annotation { "Feature Type Name" : "Feature", "Feature Type Description" : "" }
export const myFeature = defineFeature(function(context is Context, id is Id, definition is map)
    precondition{}
    {
        {
            var Q0;
            Q0=qCreatedBy(makeId("Top.planeOp"),FACE);
            var sketch = newSketch(context, id + "F0", { "sketchPlane" : qUnion([Q0])});
            skLineSegment(sketch, "E0.bottom", {"start": v(0, 0) * mm, "end": v(203.2, 0) * mm});
            skLineSegment(sketch, "E0.top", {"start": v(0, 254) * mm, "end": v(203.2, 254) * mm});
            skLineSegment(sketch, "E0.left", {"start": v(0, 0) * mm, "end": v(0, 254) * mm});
            skLineSegment(sketch, "E0.right", {"start": v(203.2, 0) * mm, "end": v(203.2, 254) * mm});
            skSolve(sketch);
        }
        {
            var Q0;
            Q0=makeQuery(id+"F0.imprint","IMPRINT",FACE,{"disambiguationData":[TD([[makeQuery(id+"F0.imprint","IMPRINT",EDGE,{"derivedFrom":sQuery(id+"F0.wireOp",EDGE,"E0.bottom")}),1.0]])]});
            extrude(context, id + "F1", {"entities" : qUnion([Q0]), "depth" : 6.35 * mm});
        }
        {
            var Q0;
            Q0=makeQuery(id+"F1.opExtrude","CAP_FACE",FACE,{"disambiguationData":[OSD([sQuery(id+"F0.wireOp",EDGE,"E0.bottom"),sQuery(id+"F0.wireOp",EDGE,"E0.top"),sQuery(id+"F0.wireOp",EDGE,"E0.left"),sQuery(id+"F0.wireOp",EDGE,"E0.right")])],"isStart":false});
            var sketch = newSketch(context, id + "F2", { "sketchPlane" : qUnion([Q0])});
            skLineSegment(sketch, "E1.bottom", {"start": v(50.8, 223.52) * mm, "end": v(152.4, 223.52) * mm});
            skLineSegment(sketch, "E1.top", {"start": v(50.8, 30.48) * mm, "end": v(152.4, 30.48) * mm});
            skLineSegment(sketch, "E1.left", {"start": v(44.45, 217.17) * mm, "end": v(44.45, 36.83) * mm});
            skLineSegment(sketch, "E1.right", {"start": v(158.75, 217.17) * mm, "end": v(158.75, 36.83) * mm});
            skPoint(sketch, "E2.visualSharp", {"position": v(44.45, 223.52) * mm});
            skArc(sketch, "E2.filletArc", {"start": v(50.8, 223.52) * mm, "mid": v(46.3, 221.66) * mm, "end": v(44.45, 217.17) * mm});
            skPoint(sketch, "E3.visualSharp", {"position": v(158.75, 223.52) * mm});
            skArc(sketch, "E3.filletArc", {"start": v(158.75, 217.17) * mm, "mid": v(156.9, 221.66) * mm, "end": v(152.4, 223.52) * mm});
            skPoint(sketch, "E4.visualSharp", {"position": v(158.75, 30.48) * mm});
            skArc(sketch, "E4.filletArc", {"start": v(152.4, 30.48) * mm, "mid": v(156.9, 32.34) * mm, "end": v(158.75, 36.83) * mm});
            skPoint(sketch, "E5.visualSharp", {"position": v(44.45, 30.48) * mm});
            skArc(sketch, "E5.filletArc", {"start": v(44.45, 36.83) * mm, "mid": v(46.3, 32.34) * mm, "end": v(50.8, 30.48) * mm});
            skSolve(sketch);
        }
        {
            var Q0;
            Q0=makeQuery(id+"F2.imprint","IMPRINT",FACE,{"disambiguationData":[TD([[makeQuery(id+"F2.imprint","IMPRINT",EDGE,{"derivedFrom":sQuery(id+"F2.wireOp",EDGE,"E1.bottom")}),-1.0]])]});
            extrude(context, id + "F3", {"entities" : qUnion([Q0]), "operationType" : NewBodyOperationType.ADD, "depth" : 50.8 * mm});
        }
        {
            var Q0;
            Q0=makeQuery(id+"F3.opExtrude","CAP_FACE",FACE,{"disambiguationData":[OSD([sQuery(id+"F2.wireOp",EDGE,"E1.bottom"),sQuery(id+"F2.wireOp",EDGE,"E1.top"),sQuery(id+"F2.wireOp",EDGE,"E1.left"),sQuery(id+"F2.wireOp",EDGE,"E1.right"),sQuery(id+"F2.wireOp",EDGE,"E2.filletArc"),sQuery(id+"F2.wireOp",EDGE,"E3.filletArc"),sQuery(id+"F2.wireOp",EDGE,"E4.filletArc"),sQuery(id+"F2.wireOp",EDGE,"E5.filletArc")])],"isStart":false});
            var sketch = newSketch(context, id + "F4", { "sketchPlane" : qUnion([Q0])});
            skLineSegment(sketch, "E6", {"start": v(101.6, 49.53) * mm, "end": v(-6.35, 49.53) * mm});
            skLineSegment(sketch, "E7", {"start": v(-6.35, 49.53) * mm, "end": v(-6.35, 328.93) * mm});
            skLineSegment(sketch, "E8", {"start": v(-6.35, 328.93) * mm, "end": v(209.55, 328.93) * mm});
            skLineSegment(sketch, "E9", {"start": v(209.55, 328.93) * mm, "end": v(209.55, 49.53) * mm});
            skLineSegment(sketch, "E10", {"start": v(101.6, 49.53) * mm, "end": v(209.55, 49.53) * mm});
            skSolve(sketch);
        }
        {
            var Q0;
            {var subQ1=sQuery(id+"F4.wireOp",EDGE,"E7");Q0=makeQuery(id+"F4.imprint","IMPRINT",FACE,{"disambiguationData":[TD([[makeQuery(id+"F4.imprint","IMPRINT",EDGE,{"derivedFrom":subQ1}),-1.0]])]});}
            var Q1;
            Q1=makeQuery(id+"F4.imprint","IMPRINT",FACE,{"disambiguationData":[TD([[makeQuery(id+"F4.imprint","IMPRINT",EDGE,{"derivedFrom":makeQuery(id+"F3.opExtrude","CAP_EDGE",EDGE,{"disambiguationData":[OSD([sQuery(id+"F2.wireOp",EDGE,"E1.bottom")])],"isStart":false})}),-1.0]])]});
            extrude(context, id + "F5", {"entities" : qUnion([Q0, Q1]), "operationType" : NewBodyOperationType.ADD, "depth" : 31.75 * mm});
        }
        {
            var Q0;
            Q0=makeQuery(id+"F5.opExtrude","SWEPT_FACE",FACE,{"disambiguationData":[OSD([sQuery(id+"F4.wireOp",EDGE,"E6"),sQuery(id+"F4.wireOp",EDGE,"E10")])]});
            var sketch = newSketch(context, id + "F6", { "sketchPlane" : qUnion([Q0])});
            skLineSegment(sketch, "E11.bottom", {"start": v(-6.35, 57.15) * mm, "end": v(209.55, 57.15) * mm});
            skLineSegment(sketch, "E11.top", {"start": v(-6.35, 82.55) * mm, "end": v(209.55, 82.55) * mm});
            skLineSegment(sketch, "E11.left", {"start": v(-6.35, 57.15) * mm, "end": v(-6.35, 82.55) * mm});
            skLineSegment(sketch, "E11.right", {"start": v(209.55, 57.15) * mm, "end": v(209.55, 82.55) * mm});
            skSolve(sketch);
        }
        {
            var Q0;
            Q0=makeQuery(id+"F6.imprint","IMPRINT",FACE,{"disambiguationData":[TD([[makeQuery(id+"F6.imprint","IMPRINT",EDGE,{"derivedFrom":sQuery(id+"F6.wireOp",EDGE,"E11.top")}),-1.0]])]});
            extrude(context, id + "F7", {"entities" : qUnion([Q0]), "operationType" : NewBodyOperationType.REMOVE, "oppositeDirection" : true, "depth" : 304.3 * mm});
        }
        {
            var Q0;
            Q0=makeQuery(id+"F5.opExtrude","CAP_FACE",FACE,{"disambiguationData":[OSD([sQuery(id+"F4.wireOp",EDGE,"E6"),sQuery(id+"F4.wireOp",EDGE,"E7"),sQuery(id+"F4.wireOp",EDGE,"E8"),sQuery(id+"F4.wireOp",EDGE,"E9"),sQuery(id+"F4.wireOp",EDGE,"E10")])],"isStart":false});
            var sketch = newSketch(context, id + "F8", { "sketchPlane" : qUnion([Q0])});
            skLineSegment(sketch, "E12.bottom", {"start": v(31.75, 62.23) * mm, "end": v(165.1, 62.23) * mm});
            skLineSegment(sketch, "E12.top", {"start": v(31.75, 204.47) * mm, "end": v(165.1, 204.47) * mm});
            skLineSegment(sketch, "E12.left", {"start": v(25.4, 68.58) * mm, "end": v(25.4, 198.12) * mm});
            skLineSegment(sketch, "E12.right", {"start": v(171.45, 68.58) * mm, "end": v(171.45, 198.12) * mm});
            skPoint(sketch, "E13.visualSharp", {"position": v(25.4, 204.47) * mm});
            skArc(sketch, "E13.filletArc", {"start": v(31.75, 204.47) * mm, "mid": v(27.26, 202.61) * mm, "end": v(25.4, 198.12) * mm});
            skPoint(sketch, "E14.visualSharp", {"position": v(171.45, 204.47) * mm});
            skArc(sketch, "E14.filletArc", {"start": v(171.45, 198.12) * mm, "mid": v(169.6, 202.61) * mm, "end": v(165.1, 204.47) * mm});
            skPoint(sketch, "E15.visualSharp", {"position": v(171.45, 62.23) * mm});
            skArc(sketch, "E15.filletArc", {"start": v(165.1, 62.23) * mm, "mid": v(169.6, 64.09) * mm, "end": v(171.45, 68.58) * mm});
            skPoint(sketch, "E16.visualSharp", {"position": v(25.4, 62.23) * mm});
            skArc(sketch, "E16.filletArc", {"start": v(25.4, 68.58) * mm, "mid": v(27.26, 64.09) * mm, "end": v(31.75, 62.23) * mm});
            skSolve(sketch);
        }
        {
            var Q0;
            Q0=makeQuery(id+"F8.imprint","IMPRINT",FACE,{"disambiguationData":[TD([[makeQuery(id+"F8.imprint","IMPRINT",EDGE,{"derivedFrom":sQuery(id+"F8.wireOp",EDGE,"E12.bottom")}),1.0]])]});
            extrude(context, id + "F9", {"entities" : qUnion([Q0]), "operationType" : NewBodyOperationType.ADD, "depth" : 25.4 * mm});
        }
        {
            var Q0;
            Q0=makeQuery(id+"F9.opExtrude","CAP_FACE",FACE,{"disambiguationData":[OSD([sQuery(id+"F8.wireOp",EDGE,"E12.bottom"),sQuery(id+"F8.wireOp",EDGE,"E12.top"),sQuery(id+"F8.wireOp",EDGE,"E12.left"),sQuery(id+"F8.wireOp",EDGE,"E12.right"),sQuery(id+"F8.wireOp",EDGE,"E13.filletArc"),sQuery(id+"F8.wireOp",EDGE,"E14.filletArc"),sQuery(id+"F8.wireOp",EDGE,"E15.filletArc"),sQuery(id+"F8.wireOp",EDGE,"E16.filletArc")])],"isStart":false});
            var sketch = newSketch(context, id + "F10", { "sketchPlane" : qUnion([Q0])});
            skLineSegment(sketch, "E17.bottom", {"start": v(63.5, 179.07) * mm, "end": v(127, 179.07) * mm});
            skLineSegment(sketch, "E17.top", {"start": v(63.5, 204.47) * mm, "end": v(127, 204.47) * mm});
            skLineSegment(sketch, "E17.left", {"start": v(63.5, 179.07) * mm, "end": v(63.5, 204.47) * mm});
            skLineSegment(sketch, "E17.right", {"start": v(127, 179.07) * mm, "end": v(127, 204.47) * mm});
            skSolve(sketch);
        }
        {
            var Q0;
            Q0=makeQuery(id+"F10.imprint","IMPRINT",FACE,{"disambiguationData":[TD([[makeQuery(id+"F10.imprint","IMPRINT",EDGE,{"derivedFrom":sQuery(id+"F10.wireOp",EDGE,"E17.bottom")}),1.0]])]});
            extrude(context, id + "F11", {"entities" : qUnion([Q0]), "operationType" : NewBodyOperationType.ADD, "depth" : 12.7 * mm});
        }
        {
            var Q0;
            Q0=makeQuery(id+"F5.opExtrude","CAP_FACE",FACE,{"disambiguationData":[OSD([sQuery(id+"F4.wireOp",EDGE,"E6"),sQuery(id+"F4.wireOp",EDGE,"E7"),sQuery(id+"F4.wireOp",EDGE,"E8"),sQuery(id+"F4.wireOp",EDGE,"E9"),sQuery(id+"F4.wireOp",EDGE,"E10")])],"isStart":false});
            var sketch = newSketch(context, id + "F12", { "sketchPlane" : qUnion([Q0])});
            skLineSegment(sketch, "E18.bottom", {"start": v(179.04, 307.91) * mm, "end": v(134.59, 307.91) * mm});
            skLineSegment(sketch, "E18.top", {"start": v(179.04, 257.11) * mm, "end": v(134.59, 257.11) * mm});
            skLineSegment(sketch, "E18.left", {"start": v(185.39, 301.56) * mm, "end": v(185.39, 263.46) * mm});
            skLineSegment(sketch, "E18.right", {"start": v(128.24, 301.56) * mm, "end": v(128.24, 263.46) * mm});
            skPoint(sketch, "E19.visualSharp", {"position": v(128.24, 307.91) * mm});
            skArc(sketch, "E19.filletArc", {"start": v(134.59, 307.91) * mm, "mid": v(130.1, 306.05) * mm, "end": v(128.24, 301.56) * mm});
            skPoint(sketch, "E20.visualSharp", {"position": v(185.39, 307.91) * mm});
            skArc(sketch, "E20.filletArc", {"start": v(185.39, 301.56) * mm, "mid": v(183.53, 306.05) * mm, "end": v(179.04, 307.91) * mm});
            skPoint(sketch, "E21.visualSharp", {"position": v(185.39, 257.11) * mm});
            skArc(sketch, "E21.filletArc", {"start": v(179.04, 257.11) * mm, "mid": v(183.53, 258.97) * mm, "end": v(185.39, 263.46) * mm});
            skPoint(sketch, "E22.visualSharp", {"position": v(128.24, 257.11) * mm});
            skArc(sketch, "E22.filletArc", {"start": v(128.24, 263.46) * mm, "mid": v(130.1, 258.97) * mm, "end": v(134.59, 257.11) * mm});
            skSolve(sketch);
        }
        {
            var Q0;
            Q0=makeQuery(id+"F12.imprint","IMPRINT",FACE,{"disambiguationData":[TD([[makeQuery(id+"F12.imprint","IMPRINT",EDGE,{"derivedFrom":sQuery(id+"F12.wireOp",EDGE,"E18.bottom")}),1.0]])]});
            extrude(context, id + "F13", {"entities" : qUnion([Q0]), "operationType" : NewBodyOperationType.ADD, "depth" : 25.4 * mm});
        }
        {
            var Q0;
            Q0=makeQuery(id+"F5.opExtrude","CAP_FACE",FACE,{"disambiguationData":[OSD([sQuery(id+"F4.wireOp",EDGE,"E6"),sQuery(id+"F4.wireOp",EDGE,"E7"),sQuery(id+"F4.wireOp",EDGE,"E8"),sQuery(id+"F4.wireOp",EDGE,"E9"),sQuery(id+"F4.wireOp",EDGE,"E10")])],"isStart":false});
            var sketch = newSketch(context, id + "F14", { "sketchPlane" : qUnion([Q0])});
            skLineSegment(sketch, "E23", {"start": v(39.34, 316.23) * mm, "end": v(83.79, 316.23) * mm});
            skLineSegment(sketch, "E24", {"start": v(90.14, 309.88) * mm, "end": v(90.14, 252.73) * mm});
            skLineSegment(sketch, "E25", {"start": v(32.99, 309.88) * mm, "end": v(32.99, 252.73) * mm});
            skLineSegment(sketch, "E26", {"start": v(39.34, 246.38) * mm, "end": v(83.79, 246.38) * mm});
            skPoint(sketch, "E27.visualSharp", {"position": v(32.99, 316.23) * mm});
            skArc(sketch, "E27.filletArc", {"start": v(39.34, 316.23) * mm, "mid": v(34.85, 314.37) * mm, "end": v(32.99, 309.88) * mm});
            skPoint(sketch, "E28.visualSharp", {"position": v(90.14, 316.23) * mm});
            skArc(sketch, "E28.filletArc", {"start": v(90.14, 309.88) * mm, "mid": v(88.28, 314.37) * mm, "end": v(83.79, 316.23) * mm});
            skPoint(sketch, "E29.visualSharp", {"position": v(90.14, 246.38) * mm});
            skArc(sketch, "E29.filletArc", {"start": v(83.79, 246.38) * mm, "mid": v(88.28, 248.24) * mm, "end": v(90.14, 252.73) * mm});
            skPoint(sketch, "E30.visualSharp", {"position": v(32.99, 246.38) * mm});
            skArc(sketch, "E30.filletArc", {"start": v(32.99, 252.73) * mm, "mid": v(34.85, 248.24) * mm, "end": v(39.34, 246.38) * mm});
            skSolve(sketch);
        }
        {
            var Q0;
            Q0=makeQuery(id+"F14.imprint","IMPRINT",FACE,{"disambiguationData":[TD([[makeQuery(id+"F14.imprint","IMPRINT",EDGE,{"derivedFrom":sQuery(id+"F14.wireOp",EDGE,"E23")}),-1.0]])]});
            extrude(context, id + "F15", {"entities" : qUnion([Q0]), "operationType" : NewBodyOperationType.ADD, "depth" : 25.4 * mm});
        }
        {
            var Q0;
            Q0=makeQuery(id+"F3.opExtrude","SWEPT_FACE",FACE,{"disambiguationData":[OSD([sQuery(id+"F2.wireOp",EDGE,"E1.top")])]});
            var sketch = newSketch(context, id + "F16", { "sketchPlane" : qUnion([Q0])});
            skText(sketch, "E31", { "text": "PDP", "fontName": "OpenSans-Bold.ttf"});
            const initialGuessF16  = {"E31": [0.06458, 0.0209, 1, 0, 0.02343]};
            skSetInitialGuess(sketch, initialGuessF16);
            skSolve(sketch);
        }
        {
            var Q0;
            Q0 = qSketchRegion(id + "F16", true);
            extrude(context, id + "F17", {"entities" : qUnion([Q0]), "operationType" : NewBodyOperationType.ADD, "depth" : 2.54 * mm});
        }
        {
            var Q0;
            Q0=makeQuery(id+"F9.opExtrude","CAP_FACE",FACE,{"disambiguationData":[OSD([sQuery(id+"F8.wireOp",EDGE,"E12.bottom"),sQuery(id+"F8.wireOp",EDGE,"E12.top"),sQuery(id+"F8.wireOp",EDGE,"E12.left"),sQuery(id+"F8.wireOp",EDGE,"E12.right"),sQuery(id+"F8.wireOp",EDGE,"E13.filletArc"),sQuery(id+"F8.wireOp",EDGE,"E14.filletArc"),sQuery(id+"F8.wireOp",EDGE,"E15.filletArc"),sQuery(id+"F8.wireOp",EDGE,"E16.filletArc")])],"isStart":false});
            var sketch = newSketch(context, id + "F18", { "sketchPlane" : qUnion([Q0])});
            skText(sketch, "E32", { "text": "Robo Rio", "fontName": "OpenSans-Bold.ttf"});
            const initialGuessF18  = {"E32": [0.03224, 0.11405, 1, 0, 0.0208]};
            skSetInitialGuess(sketch, initialGuessF18);
            skSolve(sketch);
        }
        {
            var Q0;
            Q0 = qSketchRegion(id + "F18", true);
            extrude(context, id + "F19", {"entities" : qUnion([Q0]), "operationType" : NewBodyOperationType.ADD, "depth" : 2.54 * mm});
        }
        {
            var Q0;
            Q0=makeQuery(id+"F15.opExtrude","CAP_FACE",FACE,{"disambiguationData":[OSD([sQuery(id+"F14.wireOp",EDGE,"E23"),sQuery(id+"F14.wireOp",EDGE,"E24"),sQuery(id+"F14.wireOp",EDGE,"E25"),sQuery(id+"F14.wireOp",EDGE,"E26"),sQuery(id+"F14.wireOp",EDGE,"E27.filletArc"),sQuery(id+"F14.wireOp",EDGE,"E28.filletArc"),sQuery(id+"F14.wireOp",EDGE,"E29.filletArc"),sQuery(id+"F14.wireOp",EDGE,"E30.filletArc")])],"isStart":false});
            var sketch = newSketch(context, id + "F20", { "sketchPlane" : qUnion([Q0])});
            skText(sketch, "E33", { "text": "PCM", "fontName": "OpenSans-Bold.ttf"});
            const initialGuessF20  = {"E33": [0.03537, 0.27147, 1, 0, 0.01676]};
            skSetInitialGuess(sketch, initialGuessF20);
            skSolve(sketch);
        }
        {
            var Q0;
            Q0 = qSketchRegion(id + "F20", true);
            extrude(context, id + "F21", {"entities" : qUnion([Q0]), "operationType" : NewBodyOperationType.ADD, "depth" : 2.54 * mm});
        }
        {
            var Q0;
            Q0=makeQuery(id+"F13.opExtrude","CAP_FACE",FACE,{"disambiguationData":[OSD([sQuery(id+"F12.wireOp",EDGE,"E18.bottom"),sQuery(id+"F12.wireOp",EDGE,"E18.top"),sQuery(id+"F12.wireOp",EDGE,"E18.left"),sQuery(id+"F12.wireOp",EDGE,"E18.right"),sQuery(id+"F12.wireOp",EDGE,"E19.filletArc"),sQuery(id+"F12.wireOp",EDGE,"E20.filletArc"),sQuery(id+"F12.wireOp",EDGE,"E21.filletArc"),sQuery(id+"F12.wireOp",EDGE,"E22.filletArc")])],"isStart":false});
            var sketch = newSketch(context, id + "F22", { "sketchPlane" : qUnion([Q0])});
            skText(sketch, "E34", { "text": "VRM", "fontName": "OpenSans-Bold.ttf"});
            const initialGuessF22  = {"E34": [0.13286, 0.27913, 1, 0, 0.01437]};
            skSetInitialGuess(sketch, initialGuessF22);
            skSolve(sketch);
        }
        {
            var Q0;
            Q0 = qSketchRegion(id + "F22", true);
            extrude(context, id + "F23", {"entities" : qUnion([Q0]), "operationType" : NewBodyOperationType.ADD, "depth" : 2.54 * mm});
        }
        {
            var Q0;
            Q0=makeQuery(id+"F5.opExtrude","CAP_FACE",FACE,{"disambiguationData":[OSD([sQuery(id+"F4.wireOp",EDGE,"E6"),sQuery(id+"F4.wireOp",EDGE,"E7"),sQuery(id+"F4.wireOp",EDGE,"E8"),sQuery(id+"F4.wireOp",EDGE,"E9"),sQuery(id+"F4.wireOp",EDGE,"E10")])],"isStart":false});
            var sketch = newSketch(context, id + "F24", { "sketchPlane" : qUnion([Q0])});
            skCircle(sketch, "E35", {"center": v(187.94, 69.87) * mm, "radius": 6.35 * mm});
            skSolve(sketch);
        }
        {
            var Q0;
            Q0=makeQuery(id+"F24.imprint","IMPRINT",FACE,{"disambiguationData":[TD([[makeQuery(id+"F24.imprint","IMPRINT",EDGE,{"derivedFrom":sQuery(id+"F24.wireOp",EDGE,"E35")}),1.0]])]});
            extrude(context, id + "F25", {"entities" : qUnion([Q0]), "oppositeDirection" : true, "depth" : 84.84 * mm});
        }
        {
            var Q0;
            Q0=makeQuery(id+"F5.opExtrude","CAP_FACE",FACE,{"disambiguationData":[OSD([sQuery(id+"F4.wireOp",EDGE,"E6"),sQuery(id+"F4.wireOp",EDGE,"E7"),sQuery(id+"F4.wireOp",EDGE,"E8"),sQuery(id+"F4.wireOp",EDGE,"E9"),sQuery(id+"F4.wireOp",EDGE,"E10")])],"isStart":false});
            var sketch = newSketch(context, id + "F26", { "sketchPlane" : qUnion([Q0])});
            skCircle(sketch, "E36", {"center": v(11.67, 66.64) * mm, "radius": 6.35 * mm});
            skSolve(sketch);
        }
        {
            var Q0;
            Q0=makeQuery(id+"F26.imprint","IMPRINT",FACE,{"disambiguationData":[TD([[makeQuery(id+"F26.imprint","IMPRINT",EDGE,{"derivedFrom":sQuery(id+"F26.wireOp",EDGE,"E36")}),1.0]])]});
            extrude(context, id + "F27", {"entities" : qUnion([Q0]), "oppositeDirection" : true, "depth" : 83.82 * mm});
        }
        {
            var Q0;
            Q0=makeQuery(id+"F1.opExtrude","SWEPT_FACE",FACE,{"disambiguationData":[OSD([sQuery(id+"F0.wireOp",EDGE,"E0.top")])]});
            extrude(context, id + "F28", {"entities" : qUnion([Q0]), "operationType" : NewBodyOperationType.ADD, "depth" : 75.18 * mm});
        }
        {
            var Q0;
            Q0=makeQuery(id+"F5.opExtrude","CAP_FACE",FACE,{"disambiguationData":[OSD([sQuery(id+"F4.wireOp",EDGE,"E6"),sQuery(id+"F4.wireOp",EDGE,"E7"),sQuery(id+"F4.wireOp",EDGE,"E8"),sQuery(id+"F4.wireOp",EDGE,"E9"),sQuery(id+"F4.wireOp",EDGE,"E10")])],"isStart":false});
            var sketch = newSketch(context, id + "F29", { "sketchPlane" : qUnion([Q0])});
            skCircle(sketch, "E37", {"center": v(13.2, 312.53) * mm, "radius": 6.35 * mm});
            skCircle(sketch, "E38", {"center": v(193.4, 316.08) * mm, "radius": 6.35 * mm});
            skSolve(sketch);
        }
        {
            var Q0;
            Q0=makeQuery(id+"F29.imprint","IMPRINT",FACE,{"disambiguationData":[TD([[makeQuery(id+"F29.imprint","IMPRINT",EDGE,{"derivedFrom":sQuery(id+"F29.wireOp",EDGE,"E37")}),1.0]])]});
            var Q1;
            Q1=makeQuery(id+"F29.imprint","IMPRINT",FACE,{"disambiguationData":[TD([[makeQuery(id+"F29.imprint","IMPRINT",EDGE,{"derivedFrom":sQuery(id+"F29.wireOp",EDGE,"E38")}),1.0]])]});
            extrude(context, id + "F30", {"entities" : qUnion([Q0, Q1]), "oppositeDirection" : true, "depth" : 85.1 * mm});
        }
        {
            var Q0;
            {var subQ0=sQuery(id+"F12.wireOp",EDGE,"E18.right");var subQ1=sQuery(id+"F12.wireOp",EDGE,"E18.left");var subQ2=sQuery(id+"F12.wireOp",EDGE,"E20.filletArc");var subQ3=sQuery(id+"F12.wireOp",EDGE,"E22.filletArc");var subQ4=sQuery(id+"F12.wireOp",EDGE,"E19.filletArc");var subQ5=sQuery(id+"F12.wireOp",EDGE,"E18.bottom");var subQ6=sQuery(id+"F12.wireOp",EDGE,"E21.filletArc");var subQ7=sQuery(id+"F12.wireOp",EDGE,"E18.top");Q0=makeQuery(id+"F23.boolean.opBoolean","SPLIT",FACE,{"disambiguationData":[TD([makeQuery(id+"F13.opExtrude","SWEPT_FACE",FACE,{"disambiguationData":[OSD([subQ5])]})])],"derivedFrom":makeQuery(id+"F13.opExtrude","CAP_FACE",FACE,{"disambiguationData":[OSD([subQ5,subQ7,subQ1,subQ0,subQ4,subQ2,subQ6,subQ3])],"isStart":false})});}
            var sketch = newSketch(context, id + "F31", { "sketchPlane" : qUnion([Q0])});
            skLineSegment(sketch, "E39", {"start": v(179.04, 257.11) * mm, "end": v(179.04, 260.92) * mm});
            skLineSegment(sketch, "E40", {"start": v(185.39, 263.46) * mm, "end": v(181.58, 263.46) * mm});
            skPoint(sketch, "E41.visualSharp", {"position": v(179.04, 263.46) * mm});
            skArc(sketch, "E41.filletArc", {"start": v(181.58, 263.46) * mm, "mid": v(179.78, 262.72) * mm, "end": v(179.04, 260.92) * mm});
            skSolve(sketch);
        }
        {
            var Q0;
            Q0=makeQuery(id+"F31.imprint","IMPRINT",FACE,{"disambiguationData":[TD([[makeQuery(id+"F31.imprint","IMPRINT",EDGE,{"derivedFrom":sQuery(id+"F31.wireOp",EDGE,"E39")}),-1.0]])]});
            extrude(context, id + "F32", {"entities" : qUnion([Q0]), "operationType" : NewBodyOperationType.REMOVE, "oppositeDirection" : true, "depth" : 19.05 * mm});
        }
        {
            var Q0;
            Q0=makeQuery(id+"F32.boolean.opBoolean","COPY",EDGE,{"derivedFrom":makeQuery(id+"F32.opExtrude","CAP_EDGE",EDGE,{"disambiguationData":[OSD([sQuery(id+"F31.wireOp",EDGE,"E39")])],"isStart":false})});
            var Q1;
            Q1=makeQuery(id+"F32.boolean.opBoolean","COPY",EDGE,{"derivedFrom":makeQuery(id+"F32.opExtrude","CAP_EDGE",EDGE,{"disambiguationData":[OSD([sQuery(id+"F31.wireOp",EDGE,"E40")])],"isStart":false})});
            fillet(context, id + "F33", {"entities" : qUnion([Q0, Q1]), "radius" : 0.61 * mm, "tangentPropagation" : true, "allowEdgeOverflow" : false});
        }
        {
            var Q0;
            {var subQ0=sQuery(id+"F12.wireOp",EDGE,"E18.right");var subQ1=sQuery(id+"F12.wireOp",EDGE,"E18.left");var subQ2=sQuery(id+"F12.wireOp",EDGE,"E20.filletArc");var subQ3=sQuery(id+"F12.wireOp",EDGE,"E22.filletArc");var subQ4=sQuery(id+"F12.wireOp",EDGE,"E19.filletArc");var subQ5=sQuery(id+"F12.wireOp",EDGE,"E18.bottom");var subQ6=sQuery(id+"F12.wireOp",EDGE,"E21.filletArc");var subQ7=sQuery(id+"F12.wireOp",EDGE,"E18.top");Q0=makeQuery(id+"F23.boolean.opBoolean","SPLIT",FACE,{"disambiguationData":[TD([makeQuery(id+"F13.opExtrude","SWEPT_FACE",FACE,{"disambiguationData":[OSD([subQ5])]})])],"derivedFrom":makeQuery(id+"F13.opExtrude","CAP_FACE",FACE,{"disambiguationData":[OSD([subQ5,subQ7,subQ1,subQ0,subQ4,subQ2,subQ6,subQ3])],"isStart":false})});}
            var sketch = newSketch(context, id + "F34", { "sketchPlane" : qUnion([Q0])});
            skLineSegment(sketch, "E42", {"start": v(128.24, 263.46) * mm, "end": v(132.05, 263.46) * mm});
            skLineSegment(sketch, "E43", {"start": v(134.59, 257.11) * mm, "end": v(134.59, 260.92) * mm});
            skLineSegment(sketch, "E44", {"start": v(134.59, 307.91) * mm, "end": v(134.59, 304.1) * mm});
            skLineSegment(sketch, "E45", {"start": v(132.05, 301.56) * mm, "end": v(128.24, 301.56) * mm});
            skLineSegment(sketch, "E46", {"start": v(179.04, 307.91) * mm, "end": v(179.04, 304.1) * mm});
            skLineSegment(sketch, "E47", {"start": v(181.58, 301.56) * mm, "end": v(185.39, 301.56) * mm});
            skPoint(sketch, "E48.visualSharp", {"position": v(134.59, 301.56) * mm});
            skArc(sketch, "E48.filletArc", {"start": v(132.05, 301.56) * mm, "mid": v(133.84, 302.3) * mm, "end": v(134.59, 304.1) * mm});
            skPoint(sketch, "E49.visualSharp", {"position": v(179.04, 301.56) * mm});
            skArc(sketch, "E49.filletArc", {"start": v(179.04, 304.1) * mm, "mid": v(179.78, 302.3) * mm, "end": v(181.58, 301.56) * mm});
            skPoint(sketch, "E50.visualSharp", {"position": v(134.59, 263.46) * mm});
            skArc(sketch, "E50.filletArc", {"start": v(134.59, 260.92) * mm, "mid": v(133.84, 262.72) * mm, "end": v(132.05, 263.46) * mm});
            skSolve(sketch);
        }
        {
            var Q0;
            Q0=makeQuery(id+"F34.imprint","IMPRINT",FACE,{"disambiguationData":[TD([[makeQuery(id+"F34.imprint","IMPRINT",EDGE,{"derivedFrom":sQuery(id+"F34.wireOp",EDGE,"E42")}),-1.0]])]});
            var Q1;
            Q1=makeQuery(id+"F34.imprint","IMPRINT",FACE,{"disambiguationData":[TD([[makeQuery(id+"F34.imprint","IMPRINT",EDGE,{"derivedFrom":sQuery(id+"F34.wireOp",EDGE,"E44")}),-1.0]])]});
            var Q2;
            Q2=makeQuery(id+"F34.imprint","IMPRINT",FACE,{"disambiguationData":[TD([[makeQuery(id+"F34.imprint","IMPRINT",EDGE,{"derivedFrom":sQuery(id+"F34.wireOp",EDGE,"E46")}),1.0]])]});
            extrude(context, id + "F35", {"entities" : qUnion([Q0, Q1, Q2]), "operationType" : NewBodyOperationType.REMOVE, "oppositeDirection" : true, "depth" : 19.05 * mm});
        }
        {
            var Q0;
            Q0=makeQuery(id+"F35.boolean.opBoolean","COPY",EDGE,{"derivedFrom":makeQuery(id+"F35.opExtrude","CAP_EDGE",EDGE,{"disambiguationData":[OSD([sQuery(id+"F34.wireOp",EDGE,"E42")])],"isStart":false})});
            var Q1;
            Q1=makeQuery(id+"F35.boolean.opBoolean","COPY",EDGE,{"derivedFrom":makeQuery(id+"F35.opExtrude","CAP_EDGE",EDGE,{"disambiguationData":[OSD([sQuery(id+"F34.wireOp",EDGE,"E43")])],"isStart":false})});
            fillet(context, id + "F36", {"entities" : qUnion([Q0, Q1]), "radius" : 0.6 * mm, "tangentPropagation" : true, "allowEdgeOverflow" : false});
        }
        {
            var Q0;
            Q0=makeQuery(id+"F35.boolean.opBoolean","COPY",EDGE,{"derivedFrom":makeQuery(id+"F35.opExtrude","CAP_EDGE",EDGE,{"disambiguationData":[OSD([sQuery(id+"F34.wireOp",EDGE,"E44")])],"isStart":false})});
            var Q1;
            Q1=makeQuery(id+"F35.boolean.opBoolean","COPY",EDGE,{"derivedFrom":makeQuery(id+"F35.opExtrude","CAP_EDGE",EDGE,{"disambiguationData":[OSD([sQuery(id+"F34.wireOp",EDGE,"E45")])],"isStart":false})});
            fillet(context, id + "F37", {"entities" : qUnion([Q0, Q1]), "radius" : 0.6 * mm, "tangentPropagation" : true, "allowEdgeOverflow" : false});
        }
        {
            var Q0;
            Q0=makeQuery(id+"F35.boolean.opBoolean","COPY",EDGE,{"derivedFrom":makeQuery(id+"F35.opExtrude","CAP_EDGE",EDGE,{"disambiguationData":[OSD([sQuery(id+"F34.wireOp",EDGE,"E47")])],"isStart":false})});
            var Q1;
            Q1=makeQuery(id+"F35.boolean.opBoolean","COPY",EDGE,{"derivedFrom":makeQuery(id+"F35.opExtrude","CAP_EDGE",EDGE,{"disambiguationData":[OSD([sQuery(id+"F34.wireOp",EDGE,"E46")])],"isStart":false})});
            fillet(context, id + "F38", {"entities" : qUnion([Q0, Q1]), "radius" : 0.6 * mm, "tangentPropagation" : true, "allowEdgeOverflow" : false});
        }
        {
            var Q0;
            {var subQ0=sQuery(id+"F14.wireOp",EDGE,"E27.filletArc");var subQ1=sQuery(id+"F14.wireOp",EDGE,"E30.filletArc");var subQ2=sQuery(id+"F14.wireOp",EDGE,"E28.filletArc");var subQ3=sQuery(id+"F14.wireOp",EDGE,"E29.filletArc");var subQ4=sQuery(id+"F14.wireOp",EDGE,"E23");var subQ5=sQuery(id+"F14.wireOp",EDGE,"E24");var subQ6=sQuery(id+"F14.wireOp",EDGE,"E25");var subQ7=sQuery(id+"F14.wireOp",EDGE,"E26");Q0=makeQuery(id+"F21.boolean.opBoolean","SPLIT",FACE,{"disambiguationData":[TD([makeQuery(id+"F15.opExtrude","SWEPT_FACE",FACE,{"disambiguationData":[OSD([subQ4])]})])],"derivedFrom":makeQuery(id+"F15.opExtrude","CAP_FACE",FACE,{"disambiguationData":[OSD([subQ4,subQ5,subQ6,subQ7,subQ0,subQ2,subQ3,subQ1])],"isStart":false})});}
            var sketch = newSketch(context, id + "F39", { "sketchPlane" : qUnion([Q0])});
            skLineSegment(sketch, "E51", {"start": v(39.34, 316.23) * mm, "end": v(39.34, 312.42) * mm});
            skLineSegment(sketch, "E52", {"start": v(36.8, 309.88) * mm, "end": v(32.99, 309.88) * mm});
            skLineSegment(sketch, "E53", {"start": v(32.99, 252.73) * mm, "end": v(36.8, 252.73) * mm});
            skLineSegment(sketch, "E54", {"start": v(39.34, 250.2) * mm, "end": v(39.34, 246.38) * mm});
            skLineSegment(sketch, "E55", {"start": v(83.79, 246.38) * mm, "end": v(83.79, 250.2) * mm});
            skLineSegment(sketch, "E56", {"start": v(86.33, 252.73) * mm, "end": v(90.14, 252.73) * mm});
            skLineSegment(sketch, "E57", {"start": v(83.79, 316.23) * mm, "end": v(83.79, 312.42) * mm});
            skLineSegment(sketch, "E58", {"start": v(86.33, 309.88) * mm, "end": v(90.14, 309.88) * mm});
            skPoint(sketch, "E59.visualSharp", {"position": v(39.34, 309.88) * mm});
            skArc(sketch, "E59.filletArc", {"start": v(36.8, 309.88) * mm, "mid": v(38.6, 310.62) * mm, "end": v(39.34, 312.42) * mm});
            skPoint(sketch, "E60.visualSharp", {"position": v(83.79, 309.88) * mm});
            skArc(sketch, "E60.filletArc", {"start": v(83.79, 312.42) * mm, "mid": v(84.53, 310.62) * mm, "end": v(86.33, 309.88) * mm});
            skPoint(sketch, "E61.visualSharp", {"position": v(83.79, 252.73) * mm});
            skArc(sketch, "E61.filletArc", {"start": v(86.33, 252.73) * mm, "mid": v(84.53, 251.99) * mm, "end": v(83.79, 250.2) * mm});
            skPoint(sketch, "E62.visualSharp", {"position": v(39.34, 252.73) * mm});
            skArc(sketch, "E62.filletArc", {"start": v(39.34, 250.2) * mm, "mid": v(38.6, 251.99) * mm, "end": v(36.8, 252.73) * mm});
            skSolve(sketch);
        }
        {
            var Q0;
            Q0=makeQuery(id+"F39.imprint","IMPRINT",FACE,{"disambiguationData":[TD([[makeQuery(id+"F39.imprint","IMPRINT",EDGE,{"derivedFrom":sQuery(id+"F39.wireOp",EDGE,"E55")}),-1.0]])]});
            var Q1;
            Q1=makeQuery(id+"F39.imprint","IMPRINT",FACE,{"disambiguationData":[TD([[makeQuery(id+"F39.imprint","IMPRINT",EDGE,{"derivedFrom":sQuery(id+"F39.wireOp",EDGE,"E53")}),-1.0]])]});
            var Q2;
            Q2=makeQuery(id+"F39.imprint","IMPRINT",FACE,{"disambiguationData":[TD([[makeQuery(id+"F39.imprint","IMPRINT",EDGE,{"derivedFrom":sQuery(id+"F39.wireOp",EDGE,"E51")}),-1.0]])]});
            var Q3;
            Q3=makeQuery(id+"F39.imprint","IMPRINT",FACE,{"disambiguationData":[TD([[makeQuery(id+"F39.imprint","IMPRINT",EDGE,{"derivedFrom":sQuery(id+"F39.wireOp",EDGE,"E57")}),1.0]])]});
            extrude(context, id + "F40", {"entities" : qUnion([Q0, Q1, Q2, Q3]), "operationType" : NewBodyOperationType.REMOVE, "oppositeDirection" : true, "depth" : 19.05 * mm});
        }
        {
            var Q0;
            Q0=makeQuery(id+"F40.boolean.opBoolean","COPY",EDGE,{"derivedFrom":makeQuery(id+"F40.opExtrude","CAP_EDGE",EDGE,{"disambiguationData":[OSD([sQuery(id+"F39.wireOp",EDGE,"E51")])],"isStart":false})});
            var Q1;
            Q1=makeQuery(id+"F40.boolean.opBoolean","COPY",EDGE,{"derivedFrom":makeQuery(id+"F40.opExtrude","CAP_EDGE",EDGE,{"disambiguationData":[OSD([sQuery(id+"F39.wireOp",EDGE,"E52")])],"isStart":false})});
            fillet(context, id + "F41", {"entities" : qUnion([Q0, Q1]), "radius" : 0.6 * mm, "tangentPropagation" : true, "allowEdgeOverflow" : false});
        }
        {
            var Q0;
            Q0=makeQuery(id+"F40.boolean.opBoolean","COPY",EDGE,{"derivedFrom":makeQuery(id+"F40.opExtrude","CAP_EDGE",EDGE,{"disambiguationData":[OSD([sQuery(id+"F39.wireOp",EDGE,"E58")])],"isStart":false})});
            var Q1;
            Q1=makeQuery(id+"F40.boolean.opBoolean","COPY",EDGE,{"derivedFrom":makeQuery(id+"F40.opExtrude","CAP_EDGE",EDGE,{"disambiguationData":[OSD([sQuery(id+"F39.wireOp",EDGE,"E57")])],"isStart":false})});
            fillet(context, id + "F42", {"entities" : qUnion([Q0, Q1]), "radius" : 0.6 * mm, "tangentPropagation" : true, "allowEdgeOverflow" : false});
        }
        {
            var Q0;
            Q0=makeQuery(id+"F40.boolean.opBoolean","COPY",EDGE,{"derivedFrom":makeQuery(id+"F40.opExtrude","CAP_EDGE",EDGE,{"disambiguationData":[OSD([sQuery(id+"F39.wireOp",EDGE,"E55")])],"isStart":false})});
            var Q1;
            Q1=makeQuery(id+"F40.boolean.opBoolean","COPY",EDGE,{"derivedFrom":makeQuery(id+"F40.opExtrude","CAP_EDGE",EDGE,{"disambiguationData":[OSD([sQuery(id+"F39.wireOp",EDGE,"E61.filletArc")])],"isStart":false})});
            var Q2;
            Q2=makeQuery(id+"F40.boolean.opBoolean","COPY",EDGE,{"derivedFrom":makeQuery(id+"F40.opExtrude","CAP_EDGE",EDGE,{"disambiguationData":[OSD([sQuery(id+"F39.wireOp",EDGE,"E56")])],"isStart":false})});
            fillet(context, id + "F43", {"entities" : qUnion([Q0, Q1, Q2]), "radius" : 0.6 * mm, "tangentPropagation" : true, "allowEdgeOverflow" : false});
        }
        {
            var Q0;
            Q0=makeQuery(id+"F40.boolean.opBoolean","COPY",EDGE,{"derivedFrom":makeQuery(id+"F40.opExtrude","CAP_EDGE",EDGE,{"disambiguationData":[OSD([sQuery(id+"F39.wireOp",EDGE,"E53")])],"isStart":false})});
            var Q1;
            Q1=makeQuery(id+"F40.boolean.opBoolean","COPY",EDGE,{"derivedFrom":makeQuery(id+"F40.opExtrude","CAP_EDGE",EDGE,{"disambiguationData":[OSD([sQuery(id+"F39.wireOp",EDGE,"E54")])],"isStart":false})});
            fillet(context, id + "F44", {"entities" : qUnion([Q0, Q1]), "radius" : 0.6 * mm, "tangentPropagation" : true, "allowEdgeOverflow" : false});
        }
        {
            var Q0;
            Q0=makeQuery(id+"F5.opExtrude","SWEPT_FACE",FACE,{"disambiguationData":[OSD([sQuery(id+"F4.wireOp",EDGE,"E9")])]});
            var sketch = newSketch(context, id + "F45", { "sketchPlane" : qUnion([Q0])});
            skLineSegment(sketch, "E63", {"start": v(211.26, 88.9) * mm, "end": v(236.66, 88.9) * mm});
            skLineSegment(sketch, "E64", {"start": v(236.66, 88.9) * mm, "end": v(236.66, 82.55) * mm});
            skLineSegment(sketch, "E65", {"start": v(211.26, 88.9) * mm, "end": v(211.26, 82.55) * mm});
            skLineSegment(sketch, "E66", {"start": v(211.26, 82.55) * mm, "end": v(236.66, 82.55) * mm});
            skSolve(sketch);
        }
        {
            var Q0;
            Q0=makeQuery(id+"F45.imprint","IMPRINT",FACE,{"disambiguationData":[TD([[makeQuery(id+"F45.imprint","IMPRINT",EDGE,{"derivedFrom":sQuery(id+"F45.wireOp",EDGE,"E63")}),1.0]])]});
            extrude(context, id + "F46", {"entities" : qUnion([Q0]), "operationType" : NewBodyOperationType.REMOVE, "oppositeDirection" : true, "depth" : 82.55 * mm});
        }
        {
            var Q0;
            Q0=makeQuery(id+"F5.opExtrude","SWEPT_FACE",FACE,{"disambiguationData":[OSD([sQuery(id+"F4.wireOp",EDGE,"E7")])]});
            var sketch = newSketch(context, id + "F47", { "sketchPlane" : qUnion([Q0])});
            skLineSegment(sketch, "E67", {"start": v(-238.58, 88.9) * mm, "end": v(-213.18, 88.9) * mm});
            skLineSegment(sketch, "E68", {"start": v(-213.18, 88.9) * mm, "end": v(-213.18, 82.55) * mm});
            skLineSegment(sketch, "E69", {"start": v(-238.58, 88.9) * mm, "end": v(-238.58, 82.55) * mm});
            skLineSegment(sketch, "E70", {"start": v(-238.58, 82.55) * mm, "end": v(-213.18, 82.55) * mm});
            skSolve(sketch);
        }
        {
            var Q0;
            Q0=makeQuery(id+"F47.imprint","IMPRINT",FACE,{"disambiguationData":[TD([[makeQuery(id+"F47.imprint","IMPRINT",EDGE,{"derivedFrom":sQuery(id+"F47.wireOp",EDGE,"E67")}),1.0]])]});
            extrude(context, id + "F48", {"entities" : qUnion([Q0]), "operationType" : NewBodyOperationType.REMOVE, "oppositeDirection" : true, "depth" : 88.9 * mm});
        }
    });